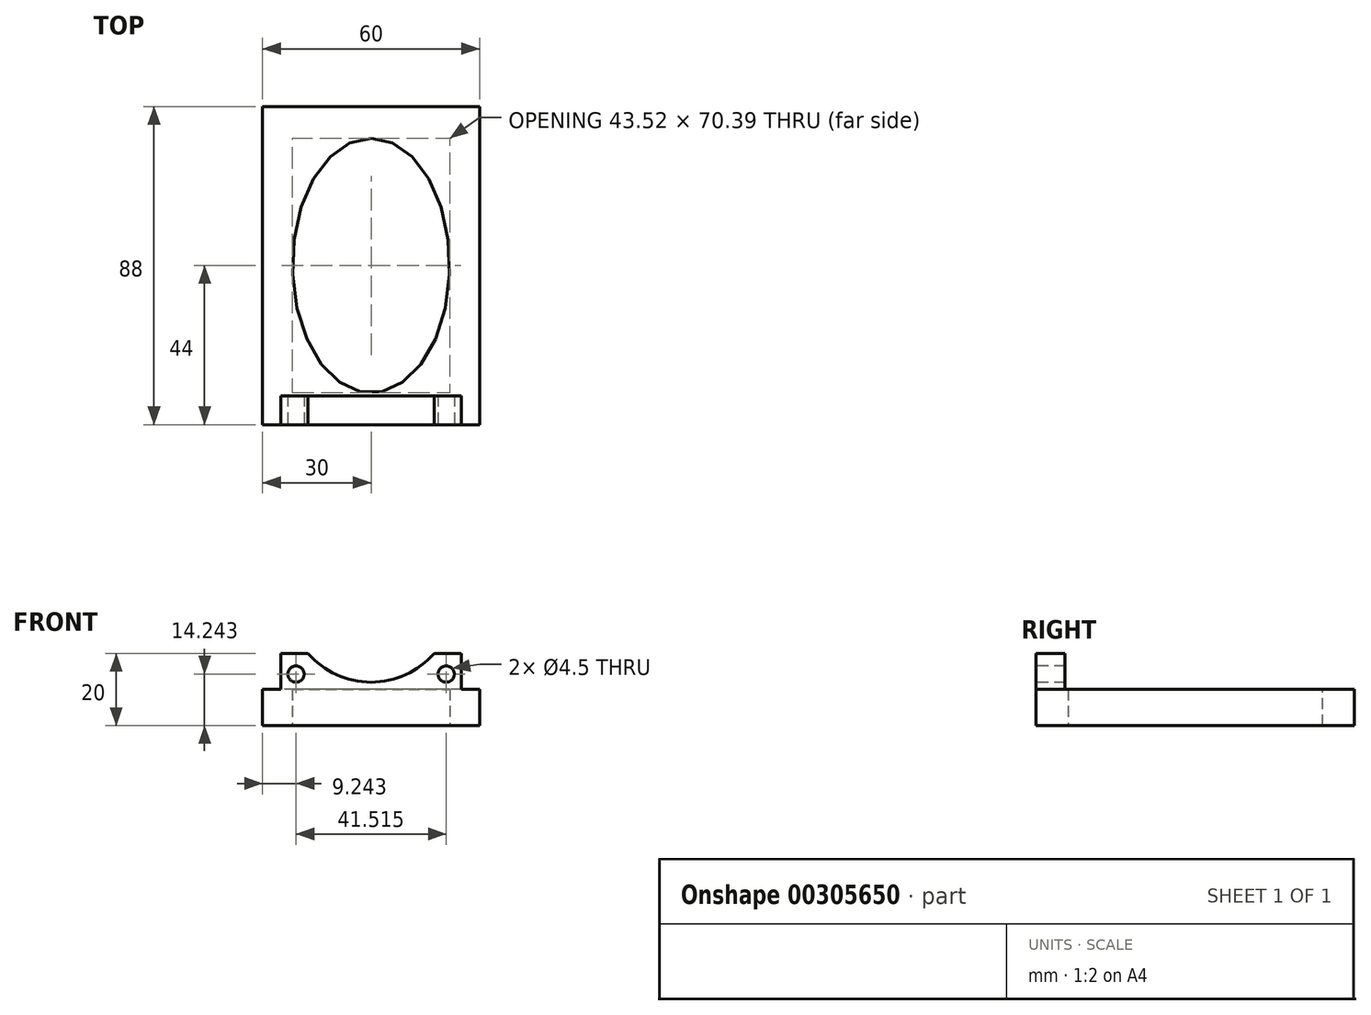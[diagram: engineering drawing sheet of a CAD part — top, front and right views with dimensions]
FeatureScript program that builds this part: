
annotation { "Feature Type Name" : "Feature", "Feature Type Description" : "" }
export const myFeature = defineFeature(function(context is Context, id is Id, definition is map)
    precondition{}
    {
        {
            var Q0;
            Q0=qCreatedBy(makeId("Front.planeOp"),FACE);
            var sketch = newSketch(context, id + "F0", { "sketchPlane" : qUnion([Q0])});
            skLineSegment(sketch, "E0.bottom", {"start": v(30, -5) * mm, "end": v(-30, -5) * mm});
            skLineSegment(sketch, "E0.top", {"start": v(30, 5) * mm, "end": v(-30, 5) * mm});
            skLineSegment(sketch, "E0.left", {"start": v(30, -5) * mm, "end": v(30, 5) * mm});
            skLineSegment(sketch, "E0.right", {"start": v(-30, -5) * mm, "end": v(-30, 5) * mm});
            skPoint(sketch, "E0.middle", {"position": v(0, 0) * mm});
            skLineSegment(sketch, "E1.top", {"start": v(25, 15) * mm, "end": v(17.44, 15) * mm});
            skLineSegment(sketch, "E1.left", {"start": v(25, 5) * mm, "end": v(25, 15) * mm});
            skLineSegment(sketch, "E2.trimOffspring", {"start": v(-25, 5) * mm, "end": v(-25, 15) * mm});
            skPoint(sketch, "E1.right.start.orphan", {"position": v(-25, -15) * mm});
            skPoint(sketch, "E3.orphan", {"position": v(25, -15) * mm});
            skLineSegment(sketch, "E4.bottom", {"start": v(-25, 5) * mm, "end": v(25, 5) * mm, "construction": true});
            skLineSegment(sketch, "E4.left", {"start": v(-25, 5) * mm, "end": v(-25, 15) * mm, "construction": true});
            skLineSegment(sketch, "E4.right", {"start": v(25, 5) * mm, "end": v(25, 15) * mm, "construction": true});
            skArc(sketch, "E5", {"start": v(-17.44, 15) * mm, "mid": v(0, 7) * mm, "end": v(17.44, 15) * mm});
            skLineSegment(sketch, "E6.trimOffspring", {"start": v(-17.44, 15) * mm, "end": v(-25, 15) * mm});
            skLineSegment(sketch, "E7.trimOffspring", {"start": v(-16.26, 13.74) * mm, "end": v(-25, 5) * mm, "construction": true});
            skLineSegment(sketch, "E8.trimOffspring", {"start": v(16.26, 13.74) * mm, "end": v(25, 5) * mm, "construction": true});
            skPoint(sketch, "E4.top.end.orphan", {"position": v(25, 55) * mm});
            skPoint(sketch, "E9.start.orphan", {"position": v(-25, 55) * mm});
            skPoint(sketch, "E10", {"position": v(-20.76, 9.24) * mm});
            skCircle(sketch, "E11", {"center": v(-20.76, 9.24) * mm, "radius": 2.25 * mm});
            skCircle(sketch, "E12.MirrorC", {"center": v(20.76, 9.24) * mm, "radius": 2.25 * mm});
            skSolve(sketch);
        }
        {
            var Q0;
            Q0=makeQuery(id+"F0.imprint","IMPRINT",FACE,{"disambiguationData":[TD([[makeQuery(id+"F0.imprint","IMPRINT",EDGE,{"derivedFrom":sQuery(id+"F0.wireOp",EDGE,"E0.bottom")}),-1.0]])]});
            extrude(context, id + "F1", {"entities" : qUnion([Q0]), "oppositeDirection" : true, "depth" : 88 * mm});
        }
        {
            var Q0;
            Q0=makeQuery(id+"F0.imprint","IMPRINT",FACE,{"disambiguationData":[TD([[makeQuery(id+"F0.imprint","IMPRINT",EDGE,{"derivedFrom":sQuery(id+"F0.wireOp",EDGE,"E1.top")}),1.0]])]});
            extrude(context, id + "F2", {"entities" : qUnion([Q0]), "operationType" : NewBodyOperationType.ADD, "oppositeDirection" : true, "depth" : 8 * mm});
        }
        {
            var Q0;
            Q0=makeQuery(id+"F1.opExtrude","SWEPT_FACE",FACE,{"disambiguationData":[OSD([sQuery(id+"F0.wireOp",EDGE,"E0.top")])]});
            var sketch = newSketch(context, id + "F3", { "sketchPlane" : qUnion([Q0])});
            skLineSegment(sketch, "E13", {"start": v(-30, 88) * mm, "end": v(30, 0) * mm, "construction": true});
            skLineSegment(sketch, "E14", {"start": v(30, 88) * mm, "end": v(-30, 0) * mm, "construction": true});
            skEllipse(sketch, "E15", {"center": v(0, 44) * mm, "majorRadius": 21.76 * mm, "minorRadius": 35.2 * mm, "majorAxis": v(1, 0)});
            skSolve(sketch);
        }
        {
            var Q0;
            Q0=makeQuery(id+"F3.imprint","IMPRINT",FACE,{"disambiguationData":[TD([[makeQuery(id+"F3.imprint","IMPRINT",EDGE,{"derivedFrom":sQuery(id+"F3.wireOp",EDGE,"E15")}),1.0]])]});
            extrude(context, id + "F4", {"entities" : qUnion([Q0]), "operationType" : NewBodyOperationType.REMOVE, "endBound" : BoundingType.THROUGH_ALL, "oppositeDirection" : true, "depth" : 25 * mm});
        }
    });
